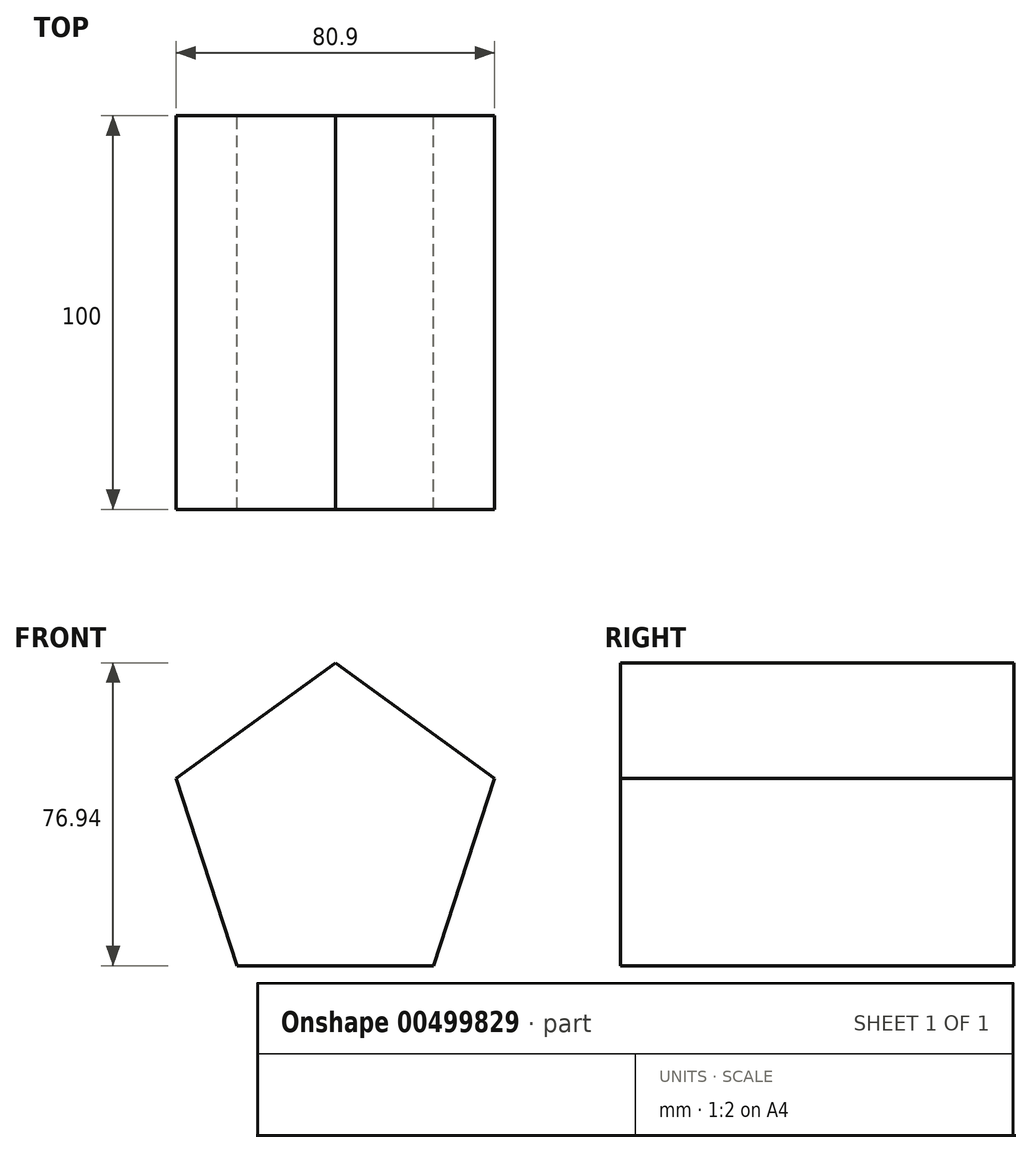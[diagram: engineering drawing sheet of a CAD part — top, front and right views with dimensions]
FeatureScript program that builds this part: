
annotation { "Feature Type Name" : "Feature", "Feature Type Description" : "" }
export const myFeature = defineFeature(function(context is Context, id is Id, definition is map)
    precondition{}
    {
        {
            var Q0;
            Q0=qCreatedBy(makeId("Front.planeOp"),FACE);
            var sketch = newSketch(context, id + "F0", { "sketchPlane" : qUnion([Q0])});
            skCircle(sketch, "E0.cCircle", {"center": v(0, 0) * mm, "radius": 34.4 * mm, "construction": true});
            skLineSegment(sketch, "E0.0", {"start": v(0, 42.53) * mm, "end": v(40.45, 13.14) * mm});
            skLineSegment(sketch, "E0.1", {"start": v(40.45, 13.14) * mm, "end": v(25, -34.4) * mm});
            skLineSegment(sketch, "E0.2", {"start": v(25, -34.4) * mm, "end": v(-25, -34.4) * mm});
            skLineSegment(sketch, "E0.3", {"start": v(-25, -34.4) * mm, "end": v(-40.45, 13.14) * mm});
            skLineSegment(sketch, "E0.4", {"start": v(-40.45, 13.14) * mm, "end": v(0, 42.53) * mm});
            skPoint(sketch, "E0.0.midPoint", {"position": v(20.23, 27.84) * mm});
            skSolve(sketch);
        }
        {
            var Q0;
            Q0 = qSketchRegion(id + "F0", true);
            extrude(context, id + "F1", {"entities" : qUnion([Q0]), "depth" : 100 * mm, "symmetric" : true});
        }
    });
